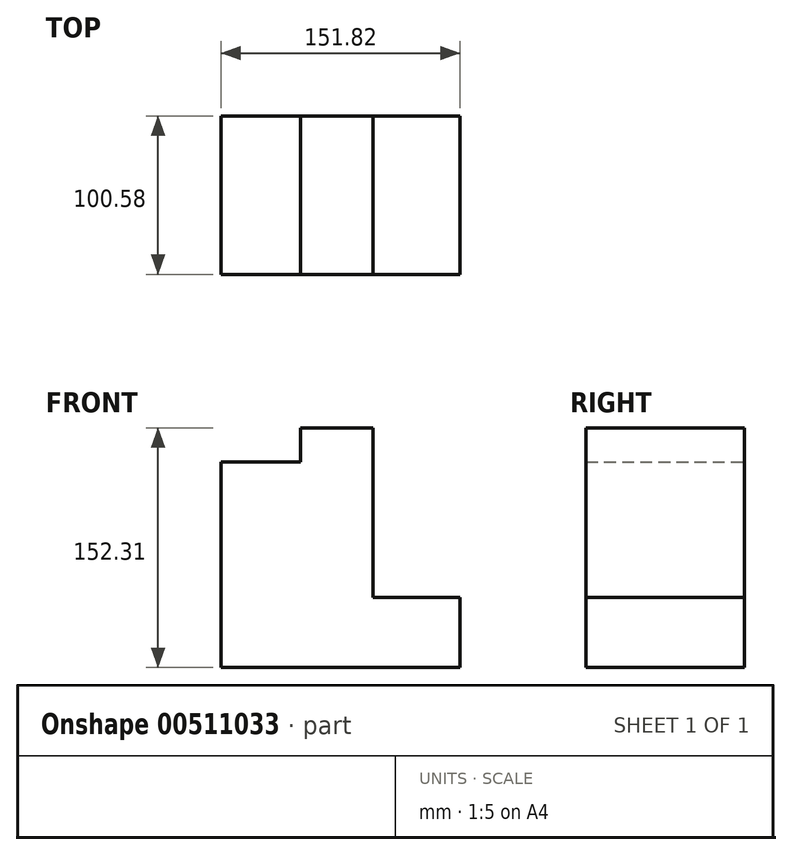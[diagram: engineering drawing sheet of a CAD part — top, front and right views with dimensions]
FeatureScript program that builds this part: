
annotation { "Feature Type Name" : "Feature", "Feature Type Description" : "" }
export const myFeature = defineFeature(function(context is Context, id is Id, definition is map)
    precondition{}
    {
        {
            var Q0;
            Q0=qCreatedBy(makeId("Front.planeOp"),FACE);
            var sketch = newSketch(context, id + "F0", { "sketchPlane" : qUnion([Q0])});
            skLineSegment(sketch, "E0.bottom", {"start": v(-75.67, 75.91) * mm, "end": v(76.15, 75.91) * mm});
            skLineSegment(sketch, "E0.top", {"start": v(-75.67, -76.4) * mm, "end": v(76.15, -76.4) * mm});
            skLineSegment(sketch, "E0.left", {"start": v(-75.67, 75.91) * mm, "end": v(-75.67, -76.4) * mm});
            skLineSegment(sketch, "E0.right", {"start": v(76.15, 75.91) * mm, "end": v(76.15, -76.4) * mm});
            skLineSegment(sketch, "E1", {"start": v(76.15, -31.81) * mm, "end": v(20.97, -31.81) * mm});
            skLineSegment(sketch, "E2", {"start": v(20.97, -31.81) * mm, "end": v(20.97, 75.91) * mm});
            skLineSegment(sketch, "E3", {"start": v(20.97, 75.91) * mm, "end": v(-25.06, 75.91) * mm});
            skLineSegment(sketch, "E4", {"start": v(-25.06, 75.91) * mm, "end": v(-25.06, 54.22) * mm});
            skLineSegment(sketch, "E5", {"start": v(-25.06, 54.22) * mm, "end": v(-75.67, 54.22) * mm});
            skSolve(sketch);
        }
        {
            var Q0;
            {var subQ1=sQuery(id+"F0.wireOp",EDGE,"E0.top");Q0=makeQuery(id+"F0.imprint","IMPRINT",FACE,{"disambiguationData":[TD([[makeQuery(id+"F0.imprint","IMPRINT",EDGE,{"derivedFrom":subQ1}),1.0]])]});}
            extrude(context, id + "F1", {"entities" : qUnion([Q0]), "depth" : 100.58 * mm});
        }
    });
